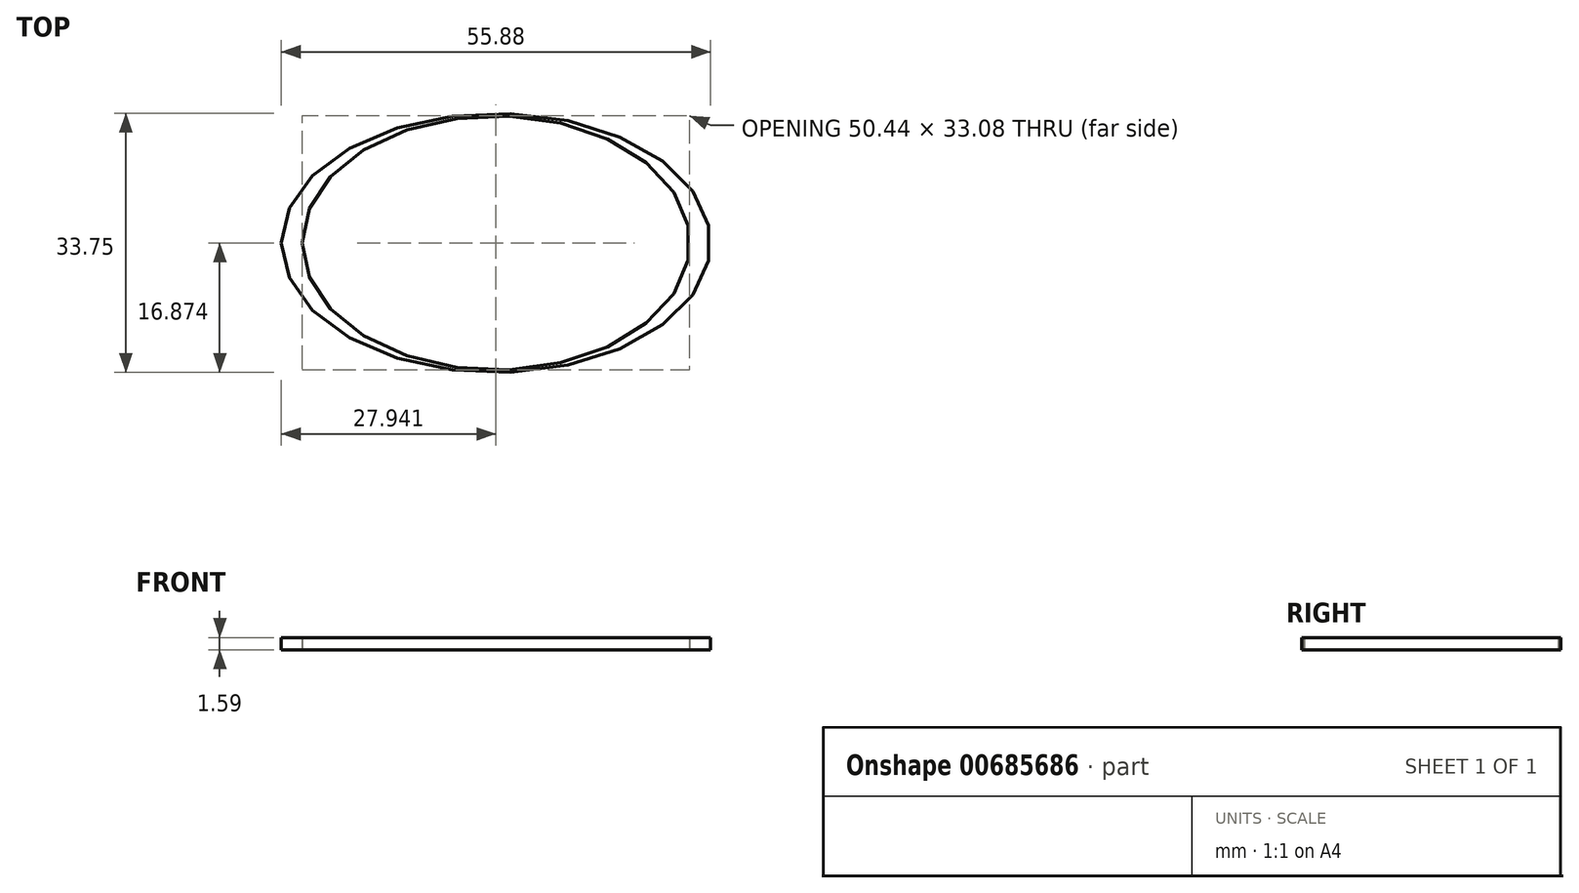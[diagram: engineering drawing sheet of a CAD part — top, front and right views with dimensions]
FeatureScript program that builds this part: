
annotation { "Feature Type Name" : "Feature", "Feature Type Description" : "" }
export const myFeature = defineFeature(function(context is Context, id is Id, definition is map)
    precondition{}
    {
        {
            var Q0;
            Q0=qCreatedBy(makeId("Top.planeOp"),FACE);
            var sketch = newSketch(context, id + "F0", { "sketchPlane" : qUnion([Q0])});
            skEllipse(sketch, "E0", {"center": v(38.3, -38) * mm, "majorRadius": 25.22 * mm, "minorRadius": 16.54 * mm, "majorAxis": v(-1, 0)});
            skEllipse(sketch, "E1", {"center": v(38.3, -38) * mm, "majorRadius": 27.94 * mm, "minorRadius": 16.88 * mm, "majorAxis": v(-1, 0)});
            skSolve(sketch);
        }
        {
            var Q0;
            Q0=makeQuery(id+"F0.imprint","IMPRINT",FACE,{"disambiguationData":[TD([[makeQuery(id+"F0.imprint","IMPRINT",EDGE,{"derivedFrom":sQuery(id+"F0.wireOp",EDGE,"E0")}),-1.0]])]});
            extrude(context, id + "F1", {"entities" : qUnion([Q0]), "depth" : 1.59 * mm, "offsetDistance" : 25.4 * mm});
        }
    });
